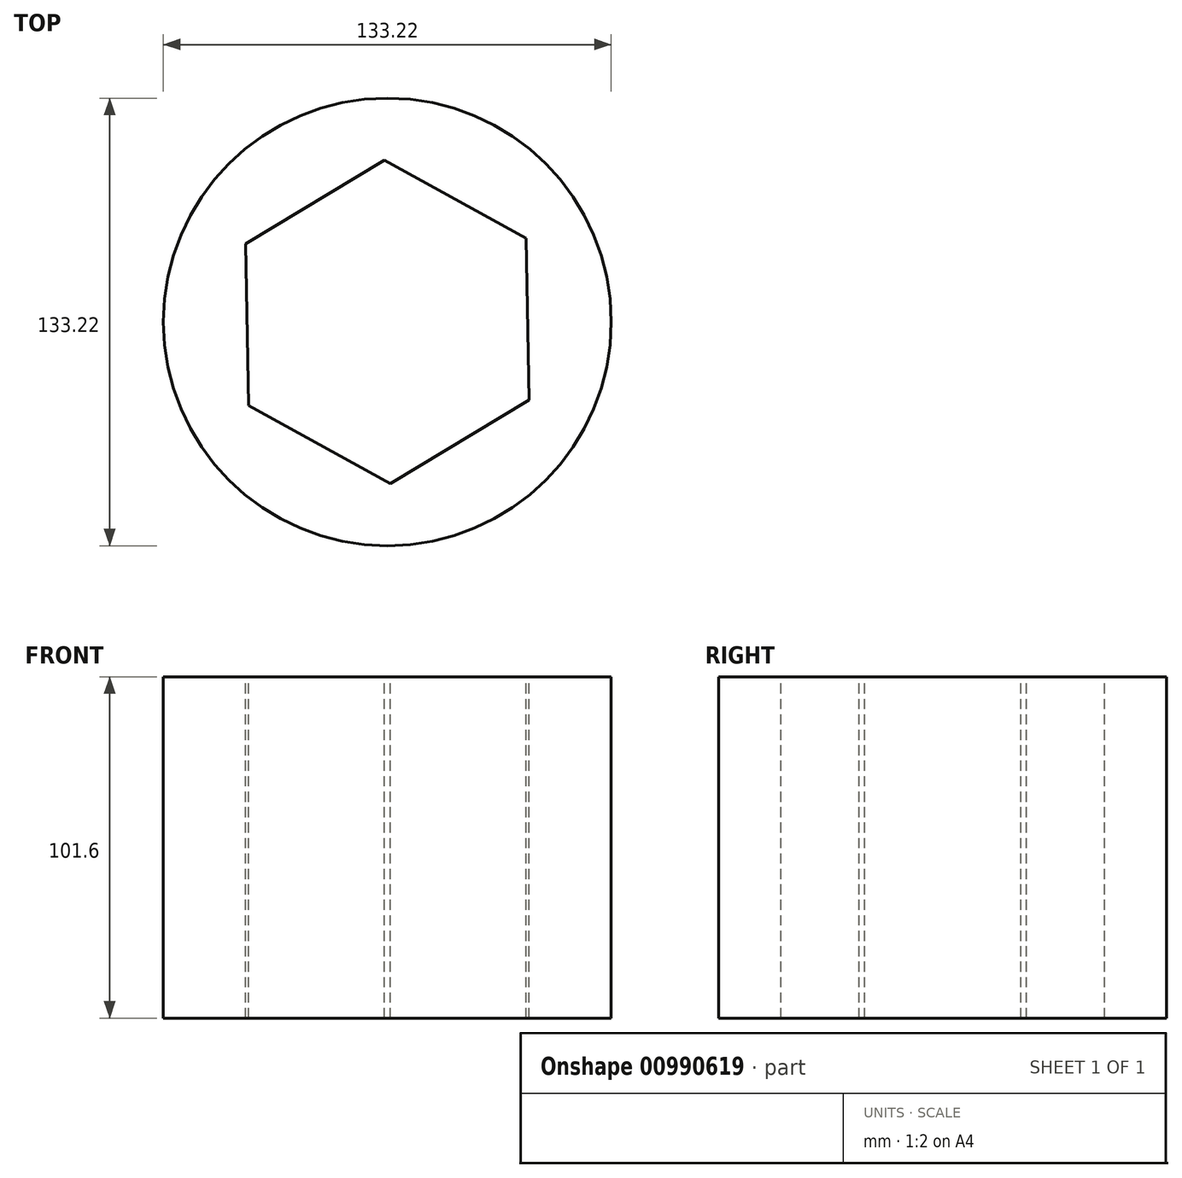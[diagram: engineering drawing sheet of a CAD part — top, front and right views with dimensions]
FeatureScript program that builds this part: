
annotation { "Feature Type Name" : "Feature", "Feature Type Description" : "" }
export const myFeature = defineFeature(function(context is Context, id is Id, definition is map)
    precondition{}
    {
        {
            var Q0;
            Q0=qCreatedBy(makeId("Top.planeOp"),FACE);
            var sketch = newSketch(context, id + "F0", { "sketchPlane" : qUnion([Q0])});
            skCircle(sketch, "E0", {"center": v(0, 0) * mm, "radius": 66.61 * mm});
            skSolve(sketch);
        }
        {
            var Q0;
            Q0 = qSketchRegion(id + "F0", true);
            extrude(context, id + "F1", {"entities" : qUnion([Q0]), "depth" : 101.6 * mm, "offsetDistance" : 25.4 * mm});
        }
        {
            var Q0;
            Q0=makeQuery(id+"F1.opExtrude","CAP_FACE",FACE,{"disambiguationData":[OSD([sQuery(id+"F0.wireOp",EDGE,"E0")])],"isStart":false});
            var sketch = newSketch(context, id + "F2", { "sketchPlane" : qUnion([Q0])});
            skCircle(sketch, "E1.cCircle", {"center": v(0, 0) * mm, "radius": 41.7 * mm, "construction": true});
            skLineSegment(sketch, "E1.0", {"start": v(-42.14, 23.28) * mm, "end": v(-0.9, 48.13) * mm});
            skLineSegment(sketch, "E1.1", {"start": v(-0.9, 48.13) * mm, "end": v(41.23, 24.85) * mm});
            skLineSegment(sketch, "E1.2", {"start": v(41.23, 24.85) * mm, "end": v(42.14, -23.28) * mm});
            skLineSegment(sketch, "E1.3", {"start": v(42.14, -23.28) * mm, "end": v(0.9, -48.13) * mm});
            skLineSegment(sketch, "E1.4", {"start": v(0.9, -48.13) * mm, "end": v(-41.23, -24.85) * mm});
            skLineSegment(sketch, "E1.5", {"start": v(-41.23, -24.85) * mm, "end": v(-42.14, 23.28) * mm});
            skPoint(sketch, "E1.0.midPoint", {"position": v(-21.52, 35.7) * mm});
            skSolve(sketch);
        }
        {
            var Q0;
            Q0=makeQuery(id+"F2.imprint","IMPRINT",FACE,{"disambiguationData":[TD([[makeQuery(id+"F2.imprint","IMPRINT",EDGE,{"derivedFrom":sQuery(id+"F2.wireOp",EDGE,"E1.0")}),-1.0]])]});
            extrude(context, id + "F3", {"entities" : qUnion([Q0]), "operationType" : NewBodyOperationType.REMOVE, "oppositeDirection" : true, "depth" : 108.7 * mm, "offsetDistance" : 25.4 * mm});
        }
    });
